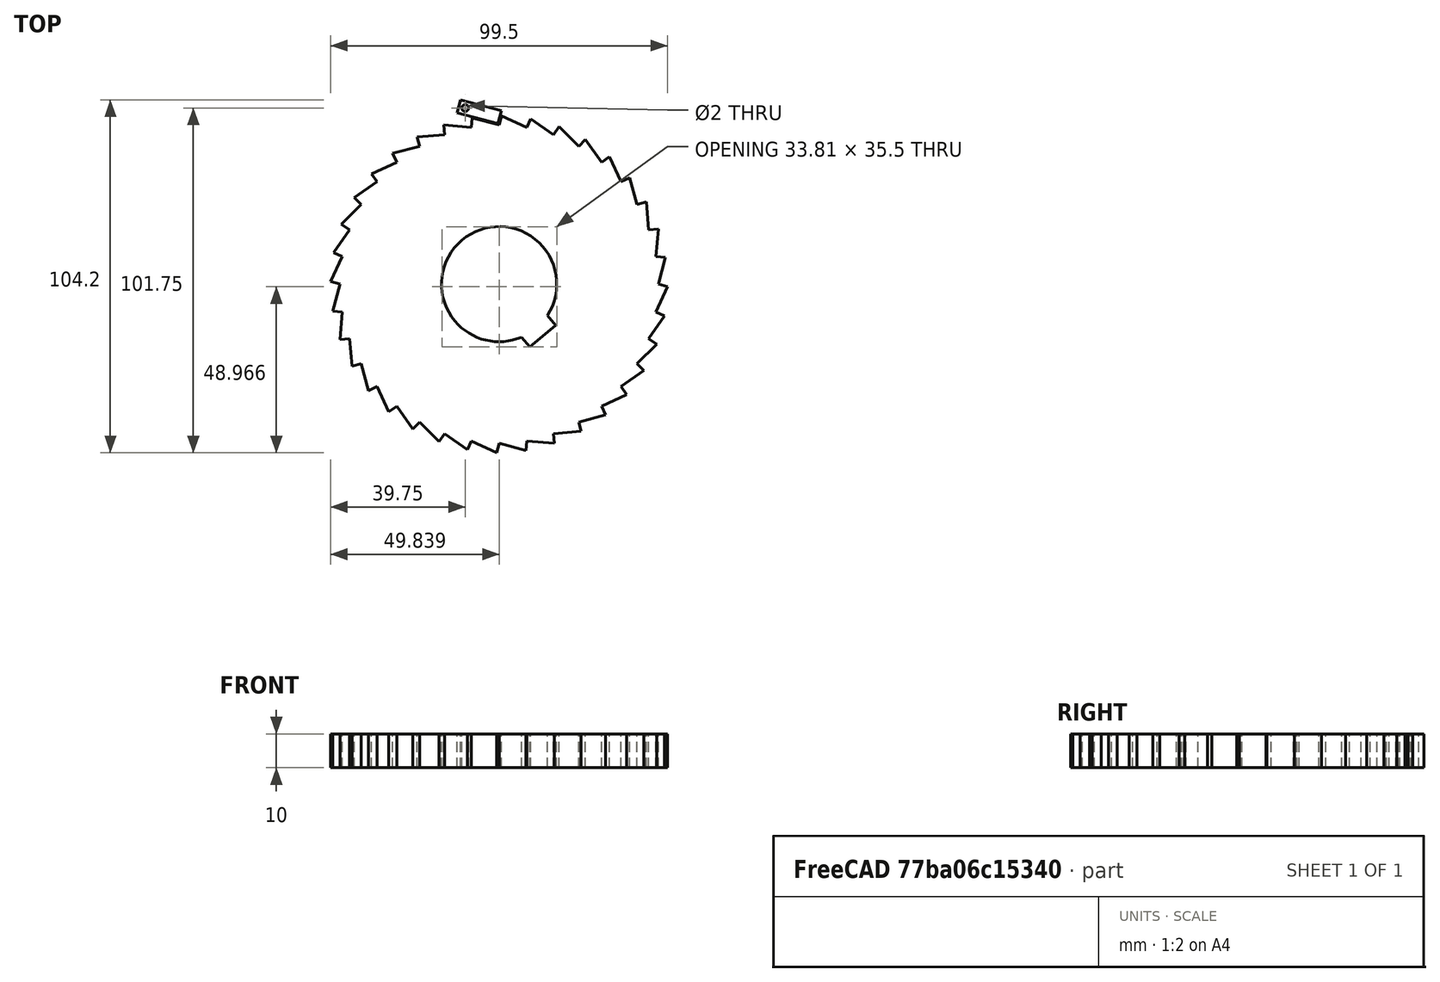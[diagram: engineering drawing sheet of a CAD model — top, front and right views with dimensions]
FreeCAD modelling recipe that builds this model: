
FCSTD DOCUMENT  (FreeCAD 0.18.2R)
Label: RATCHET
License: All rights reserved
LicenseURL: http://en.wikipedia.org/wiki/All_rights_reserved
objects: Part::Cylinder×3, Part::Box×3, Part::Cut×3, App::DocumentObjectGroupPython×3, Part::FeaturePython×1, Part::MultiFuse×1
note: 11 computed .brp shape members not serialized (recipe doc carries the construction recipe); baked Part::Feature solids carry a one-line shape summary decoded from their .brp

FEATURE [Part::Cylinder] Cylinder
  Angle = 360
  AttacherType = Attacher::AttachEngine3D
  Height = 10
  Radius = 50
FEATURE [Part::Box] Box  label="Cube"
  AttacherType = Attacher::AttachEngine3D
  Height = 10
  Length = 10
  Placement = pos=(0,47,0) rot=(0,0,1;1.309rad)
  Width = 10
FEATURE [Part::FeaturePython] Array  # Draft array (typed FeaturePython)
  Angle = 360
  ArrayType = 1
  Axis = (0,0,1)
  Base = -> Box
  Center = (0,0,0)
  Fuse = true
  IntervalAxis = (0,0,0)
  IntervalX = (1,0,0)
  IntervalY = (0,1,0)
  IntervalZ = (0,0,1)
  NumberPolar = 36
  NumberX = 2
  NumberY = 2
  NumberZ = 1
FEATURE [Part::Cut] Cut
  Base = -> Cylinder
  Tool = -> Array
FEATURE [Part::Cylinder] Cylinder001
  Angle = 360
  AttacherType = Attacher::AttachEngine3D
  Height = 10
  Radius = 17
FEATURE [Part::Box] Box001  label="Cube001"
  AttacherType = Attacher::AttachEngine3D
  Height = 10
  Length = 10
  Placement = pos=(-5,10,0) rot=(0,0,1;0rad)
  Width = 10
FEATURE [Part::MultiFuse] Fusion
  Shapes = -> [Box001,Cylinder001]
FEATURE [Part::Cut] Cut001
  Base = -> Cut
  Placement = pos=(0,0,0) rot=(0,0,1;3.83972rad)
  Tool = -> Fusion
FEATURE [Part::Box] Box002  label="Cube002"
  AttacherType = Attacher::AttachEngine3D
  Height = 10
  Length = 12.5
  Placement = pos=(-2,-2,0) rot=(0,0,1;0rad)
  Width = 4
FEATURE [Part::Cylinder] Cylinder002
  Angle = 360
  AttacherType = Attacher::AttachEngine3D
  Height = 10
  Radius = 1
FEATURE [Part::Cut] Cut002
  Base = -> Box002
  Placement = pos=(-10,52,0) rot=(0,0,1;6.02139rad)
  Tool = -> Cylinder002
FEATURE [App::DocumentObjectGroupPython] My_Placer  # scripted group (container) (typed FeaturePython)
  Placement = pos=(0,0,0) rot=(0,0,1;-2.44346rad)
  RotAxis = (0,0,1)
  RotCenter = (0,0,0)
  arc = -time*1000/6
  arc0 = 0
  arc1 = 90
  target = -> Cut001
  time = 0.84
  x = 0
  x0 = 0
  x1 = 200
  y = 0
  y0 = 0
  y1 = 0
  z = 0
  z0 = 0
  z1 = 0
FEATURE [App::DocumentObjectGroupPython] My_Placer001  # scripted group (container) (typed FeaturePython)
  Placement = pos=(-10,52,0) rot=(0,0,1;-0.261799rad)
  RotAxis = (0,0,1)
  RotCenter = (0,0,0)
  arc = -15*x0
  arc0 = 0
  arc1 = 90
  target = -> Cut002
  time = 0.84
  x = -10
  x0 = 1
  x1 = 200
  y = 52
  y0 = 0
  y1 = 0
  z = 0
  z0 = 0
  z1 = 0
  expr: x0 = cos(time * 3000) ^ 2
FEATURE [App::DocumentObjectGroupPython] My_Manager  # scripted group (container) (typed FeaturePython)
  Group = -> [My_Placer,My_Placer001]
  intervall = 1000
  sleeptime = 0.02
  start = 0
  step = 84
  text = NO
